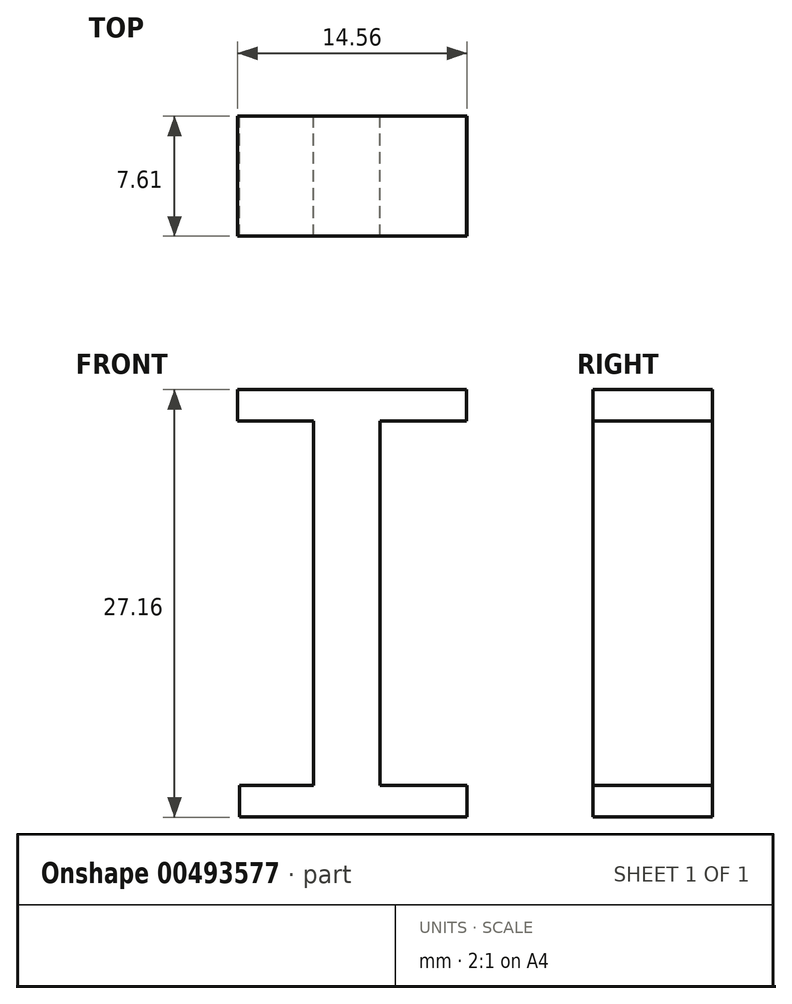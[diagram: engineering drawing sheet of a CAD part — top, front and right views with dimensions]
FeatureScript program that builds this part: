
annotation { "Feature Type Name" : "Feature", "Feature Type Description" : "" }
export const myFeature = defineFeature(function(context is Context, id is Id, definition is map)
    precondition{}
    {
        {
            var Q0;
            Q0=qCreatedBy(makeId("Front.planeOp"),FACE);
            var sketch = newSketch(context, id + "F0", { "sketchPlane" : qUnion([Q0])});
            skLineSegment(sketch, "E0.bottom", {"start": v(2.1, -11.58) * mm, "end": v(-2.1, -11.58) * mm});
            skLineSegment(sketch, "E0.top", {"start": v(2.1, 11.58) * mm, "end": v(-2.1, 11.58) * mm});
            skLineSegment(sketch, "E0.left", {"start": v(2.1, -11.58) * mm, "end": v(2.1, 11.58) * mm});
            skLineSegment(sketch, "E0.right", {"start": v(-2.1, -11.58) * mm, "end": v(-2.1, 11.58) * mm});
            skPoint(sketch, "E0.middle", {"position": v(0, 0) * mm});
            skSolve(sketch);
        }
        {
            var Q0;
            Q0=makeQuery(id+"F0.imprint","IMPRINT",FACE,{"disambiguationData":[TD([[makeQuery(id+"F0.imprint","IMPRINT",EDGE,{"derivedFrom":sQuery(id+"F0.wireOp",EDGE,"E0.bottom")}),-1.0]])]});
            extrude(context, id + "F1", {"entities" : qUnion([Q0]), "depth" : 7.61 * mm});
        }
        {
            var Q0;
            Q0=makeQuery(id+"F1.opExtrude","SWEPT_FACE",FACE,{"disambiguationData":[OSD([sQuery(id+"F0.wireOp",EDGE,"E0.top")])]});
            var sketch = newSketch(context, id + "F2", { "sketchPlane" : qUnion([Q0])});
            skLineSegment(sketch, "E1.bottom", {"start": v(0, 0) * mm, "end": v(7.6, 0) * mm});
            skLineSegment(sketch, "E1.top", {"start": v(0, -7.61) * mm, "end": v(7.6, -7.61) * mm});
            skLineSegment(sketch, "E1.left", {"start": v(0, 0) * mm, "end": v(0, -7.61) * mm});
            skLineSegment(sketch, "E1.right", {"start": v(7.6, 0) * mm, "end": v(7.6, -7.61) * mm});
            skSolve(sketch);
        }
        {
            var Q0;
            {var subQ3=sQuery(id+"F2.wireOp",EDGE,"E1.left");Q0=makeQuery(id+"F2.imprint","IMPRINT",FACE,{"disambiguationData":[TD([[makeQuery(id+"F2.imprint","IMPRINT",EDGE,{"derivedFrom":subQ3}),1.0]])]});}
            var Q1;
            {var subQ2=sQuery(id+"F2.wireOp",EDGE,"E1.right");Q1=makeQuery(id+"F2.imprint","IMPRINT",FACE,{"disambiguationData":[TD([[makeQuery(id+"F2.imprint","IMPRINT",EDGE,{"derivedFrom":subQ2}),-1.0]])]});}
            extrude(context, id + "F3", {"entities" : qUnion([Q0, Q1]), "operationType" : NewBodyOperationType.ADD, "depth" : 2 * mm});
        }
        {
            var Q0;
            Q0=makeQuery(id+"F1.opExtrude","SWEPT_FACE",FACE,{"disambiguationData":[OSD([sQuery(id+"F0.wireOp",EDGE,"E0.top")])]});
            var sketch = newSketch(context, id + "F4", { "sketchPlane" : qUnion([Q0])});
            skLineSegment(sketch, "E2.bottom", {"start": v(0, 0) * mm, "end": v(-6.93, 0) * mm});
            skLineSegment(sketch, "E2.top", {"start": v(0, -7.61) * mm, "end": v(-6.93, -7.61) * mm});
            skLineSegment(sketch, "E2.left", {"start": v(0, 0) * mm, "end": v(0, -7.61) * mm});
            skLineSegment(sketch, "E2.right", {"start": v(-6.93, 0) * mm, "end": v(-6.93, -7.61) * mm});
            skSolve(sketch);
        }
        {
            var Q0;
            {var subQ2=sQuery(id+"F4.wireOp",EDGE,"E2.right");Q0=makeQuery(id+"F4.imprint","IMPRINT",FACE,{"disambiguationData":[TD([[makeQuery(id+"F4.imprint","IMPRINT",EDGE,{"derivedFrom":subQ2}),1.0]])]});}
            var Q1;
            {var subQ2=sQuery(id+"F4.wireOp",EDGE,"E2.left");Q1=makeQuery(id+"F4.imprint","IMPRINT",FACE,{"disambiguationData":[TD([[makeQuery(id+"F4.imprint","IMPRINT",EDGE,{"derivedFrom":subQ2}),-1.0]])]});}
            extrude(context, id + "F5", {"entities" : qUnion([Q0, Q1]), "operationType" : NewBodyOperationType.ADD, "depth" : 2 * mm});
        }
        {
            var Q0;
            Q0=makeQuery(id+"F1.opExtrude","SWEPT_FACE",FACE,{"disambiguationData":[OSD([sQuery(id+"F0.wireOp",EDGE,"E0.bottom")])]});
            var sketch = newSketch(context, id + "F6", { "sketchPlane" : qUnion([Q0])});
            skPoint(sketch, "E3.oppositeSnap0", {"position": v(0, 7.61) * mm});
            skLineSegment(sketch, "E3.bottom", {"start": v(0, 0) * mm, "end": v(7.63, 0) * mm});
            skLineSegment(sketch, "E3.top", {"start": v(0, 7.61) * mm, "end": v(7.63, 7.61) * mm});
            skLineSegment(sketch, "E3.left", {"start": v(0, 0) * mm, "end": v(0, 7.61) * mm});
            skLineSegment(sketch, "E3.right", {"start": v(7.63, 0) * mm, "end": v(7.63, 7.61) * mm});
            skSolve(sketch);
        }
        {
            var Q0;
            {var subQ3=sQuery(id+"F6.wireOp",EDGE,"E3.left");Q0=makeQuery(id+"F6.imprint","IMPRINT",FACE,{"disambiguationData":[TD([[makeQuery(id+"F6.imprint","IMPRINT",EDGE,{"derivedFrom":subQ3}),-1.0]])]});}
            var Q1;
            {var subQ2=sQuery(id+"F6.wireOp",EDGE,"E3.right");Q1=makeQuery(id+"F6.imprint","IMPRINT",FACE,{"disambiguationData":[TD([[makeQuery(id+"F6.imprint","IMPRINT",EDGE,{"derivedFrom":subQ2}),1.0]])]});}
            extrude(context, id + "F7", {"entities" : qUnion([Q0, Q1]), "operationType" : NewBodyOperationType.ADD, "depth" : 2 * mm});
        }
        {
            var Q0;
            Q0=makeQuery(id+"F1.opExtrude","SWEPT_FACE",FACE,{"disambiguationData":[OSD([sQuery(id+"F0.wireOp",EDGE,"E0.bottom")])]});
            var sketch = newSketch(context, id + "F8", { "sketchPlane" : qUnion([Q0])});
            skLineSegment(sketch, "E4.bottom", {"start": v(0, 7.61) * mm, "end": v(-6.8, 7.61) * mm});
            skLineSegment(sketch, "E4.top", {"start": v(0, 0) * mm, "end": v(-6.8, 0) * mm});
            skLineSegment(sketch, "E4.left", {"start": v(0, 7.61) * mm, "end": v(0, 0) * mm});
            skLineSegment(sketch, "E4.right", {"start": v(-6.8, 7.61) * mm, "end": v(-6.8, 0) * mm});
            skSolve(sketch);
        }
        {
            var Q0;
            {var subQ2=sQuery(id+"F8.wireOp",EDGE,"E4.left");Q0=makeQuery(id+"F8.imprint","IMPRINT",FACE,{"disambiguationData":[TD([[makeQuery(id+"F8.imprint","IMPRINT",EDGE,{"derivedFrom":subQ2}),1.0]])]});}
            var Q1;
            {var subQ2=sQuery(id+"F8.wireOp",EDGE,"E4.right");Q1=makeQuery(id+"F8.imprint","IMPRINT",FACE,{"disambiguationData":[TD([[makeQuery(id+"F8.imprint","IMPRINT",EDGE,{"derivedFrom":subQ2}),1.0]])]});}
            extrude(context, id + "F9", {"entities" : qUnion([Q0, Q1]), "operationType" : NewBodyOperationType.ADD, "depth" : 2 * mm});
        }
    });
